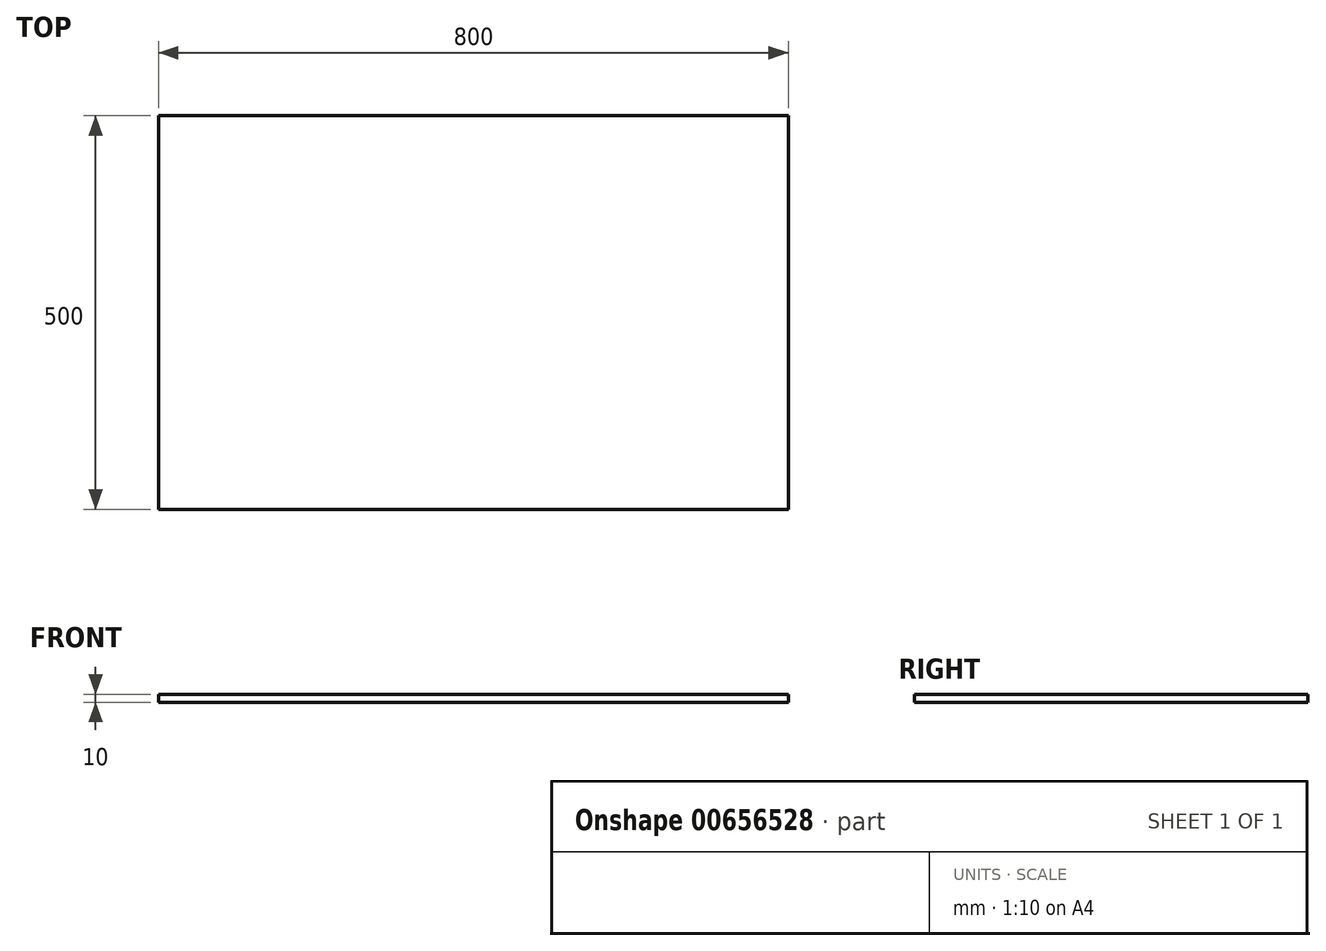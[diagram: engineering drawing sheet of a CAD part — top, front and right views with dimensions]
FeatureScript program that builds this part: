
annotation { "Feature Type Name" : "Feature", "Feature Type Description" : "" }
export const myFeature = defineFeature(function(context is Context, id is Id, definition is map)
    precondition{}
    {
        {
            var Q0;
            Q0=qCreatedBy(makeId("Top.planeOp"),FACE);
            var sketch = newSketch(context, id + "F0", { "sketchPlane" : qUnion([Q0])});
            skLineSegment(sketch, "E0.bottom", {"start": v(-120.87, 468.34) * mm, "end": v(679.13, 468.34) * mm});
            skLineSegment(sketch, "E0.top", {"start": v(-120.87, -31.66) * mm, "end": v(679.13, -31.66) * mm});
            skLineSegment(sketch, "E0.left", {"start": v(-120.87, 468.34) * mm, "end": v(-120.87, -31.66) * mm});
            skLineSegment(sketch, "E0.right", {"start": v(679.13, 468.34) * mm, "end": v(679.13, -31.66) * mm});
            skLineSegment(sketch, "E1", {"start": v(679.13, -31.66) * mm, "end": v(78.7, -31.66) * mm});
            skLineSegment(sketch, "E2", {"start": v(78.7, -31.66) * mm, "end": v(78.7, -12.07) * mm, "construction": true});
            skLineSegment(sketch, "E3", {"start": v(-120.87, -31.66) * mm, "end": v(-80.44, -31.66) * mm});
            skLineSegment(sketch, "E4", {"start": v(-80.44, -31.66) * mm, "end": v(-80.44, -11.78) * mm, "construction": true});
            skLineSegment(sketch, "E5", {"start": v(-80.44, -31.66) * mm, "end": v(0, -31.66) * mm});
            skLineSegment(sketch, "E6", {"start": v(0, -31.66) * mm, "end": v(0, -11.5) * mm, "construction": true});
            skSolve(sketch);
        }
        {
            var Q0;
            Q0=makeQuery(id+"F0.imprint","IMPRINT",FACE,{"disambiguationData":[TD([[makeQuery(id+"F0.imprint","IMPRINT",EDGE,{"derivedFrom":sQuery(id+"F0.wireOp",EDGE,"E0.bottom")}),-1.0]])]});
            extrude(context, id + "F1", {"entities" : qUnion([Q0]), "depth" : 10 * mm, "offsetDistance" : 25 * mm});
        }
    });
